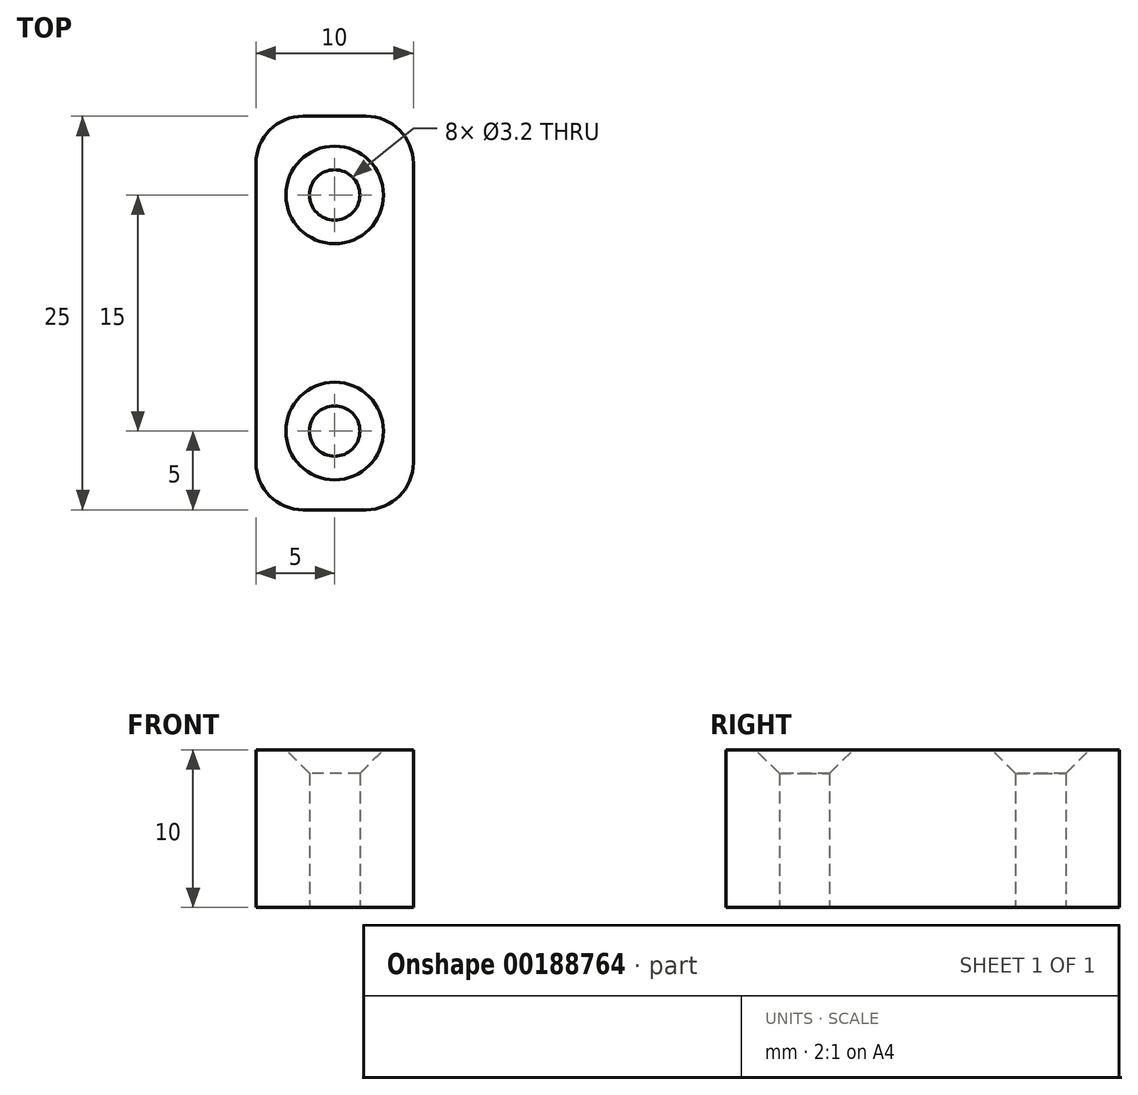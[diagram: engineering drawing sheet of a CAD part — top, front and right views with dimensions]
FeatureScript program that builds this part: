
annotation { "Feature Type Name" : "Feature", "Feature Type Description" : "" }
export const myFeature = defineFeature(function(context is Context, id is Id, definition is map)
    precondition{}
    {
        {
            var Q0;
            Q0=qCreatedBy(makeId("Top.planeOp"),FACE);
            var sketch = newSketch(context, id + "F0", { "sketchPlane" : qUnion([Q0])});
            skLineSegment(sketch, "E0.bottom", {"start": v(5, -12.5) * mm, "end": v(-5, -12.5) * mm});
            skLineSegment(sketch, "E0.top", {"start": v(5, 12.5) * mm, "end": v(-5, 12.5) * mm});
            skLineSegment(sketch, "E0.left", {"start": v(5, -12.5) * mm, "end": v(5, 12.5) * mm});
            skLineSegment(sketch, "E0.right", {"start": v(-5, -12.5) * mm, "end": v(-5, 12.5) * mm});
            skPoint(sketch, "E0.middle", {"position": v(0, 0) * mm});
            skCircle(sketch, "E1", {"center": v(0, 7.5) * mm, "radius": 1.6 * mm});
            skCircle(sketch, "E2", {"center": v(0, -7.5) * mm, "radius": 1.6 * mm});
            skLineSegment(sketch, "E3", {"start": v(-5, 0) * mm, "end": v(5, 0) * mm, "construction": true});
            skSolve(sketch);
        }
        {
            var Q0;
            Q0=makeQuery(id+"F0.imprint","IMPRINT",FACE,{"disambiguationData":[TD([[makeQuery(id+"F0.imprint","IMPRINT",EDGE,{"derivedFrom":sQuery(id+"F0.wireOp",EDGE,"E0.bottom")}),-1.0]])]});
            extrude(context, id + "F1", {"entities" : qUnion([Q0]), "depth" : 10 * mm, "offsetDistance" : 25 * mm});
        }
        {
            var Q0;
            Q0=makeQuery(id+"F1.opExtrude","SWEPT_EDGE",EDGE,{"disambiguationData":[OSD([sQuery(id+"F0.wireOp",EDGE,"E0.top"),sQuery(id+"F0.wireOp",EDGE,"E0.right")])]});
            var Q1;
            Q1=makeQuery(id+"F1.opExtrude","SWEPT_EDGE",EDGE,{"disambiguationData":[OSD([sQuery(id+"F0.wireOp",EDGE,"E0.bottom"),sQuery(id+"F0.wireOp",EDGE,"E0.right")])]});
            var Q2;
            Q2=makeQuery(id+"F1.opExtrude","SWEPT_EDGE",EDGE,{"disambiguationData":[OSD([sQuery(id+"F0.wireOp",EDGE,"E0.bottom"),sQuery(id+"F0.wireOp",EDGE,"E0.left")])]});
            var Q3;
            Q3=makeQuery(id+"F1.opExtrude","SWEPT_EDGE",EDGE,{"disambiguationData":[OSD([sQuery(id+"F0.wireOp",EDGE,"E0.top"),sQuery(id+"F0.wireOp",EDGE,"E0.left")])]});
            fillet(context, id + "F2", {"entities" : qUnion([Q0, Q1, Q2, Q3]), "radius" : 3 * mm, "tangentPropagation" : true, "allowEdgeOverflow" : false});
        }
        {
            var Q0;
            Q0=makeQuery(id+"F1.opExtrude","CAP_EDGE",EDGE,{"disambiguationData":[OSD([sQuery(id+"F0.wireOp",EDGE,"E1")])],"isStart":false});
            var Q1;
            Q1=makeQuery(id+"F1.opExtrude","CAP_EDGE",EDGE,{"disambiguationData":[OSD([sQuery(id+"F0.wireOp",EDGE,"E2")])],"isStart":false});
            chamfer(context, id + "F3", {"entities" : qUnion([Q0, Q1]), "width" : 1.5 * mm, "tangentPropagation" : true});
        }
    });
